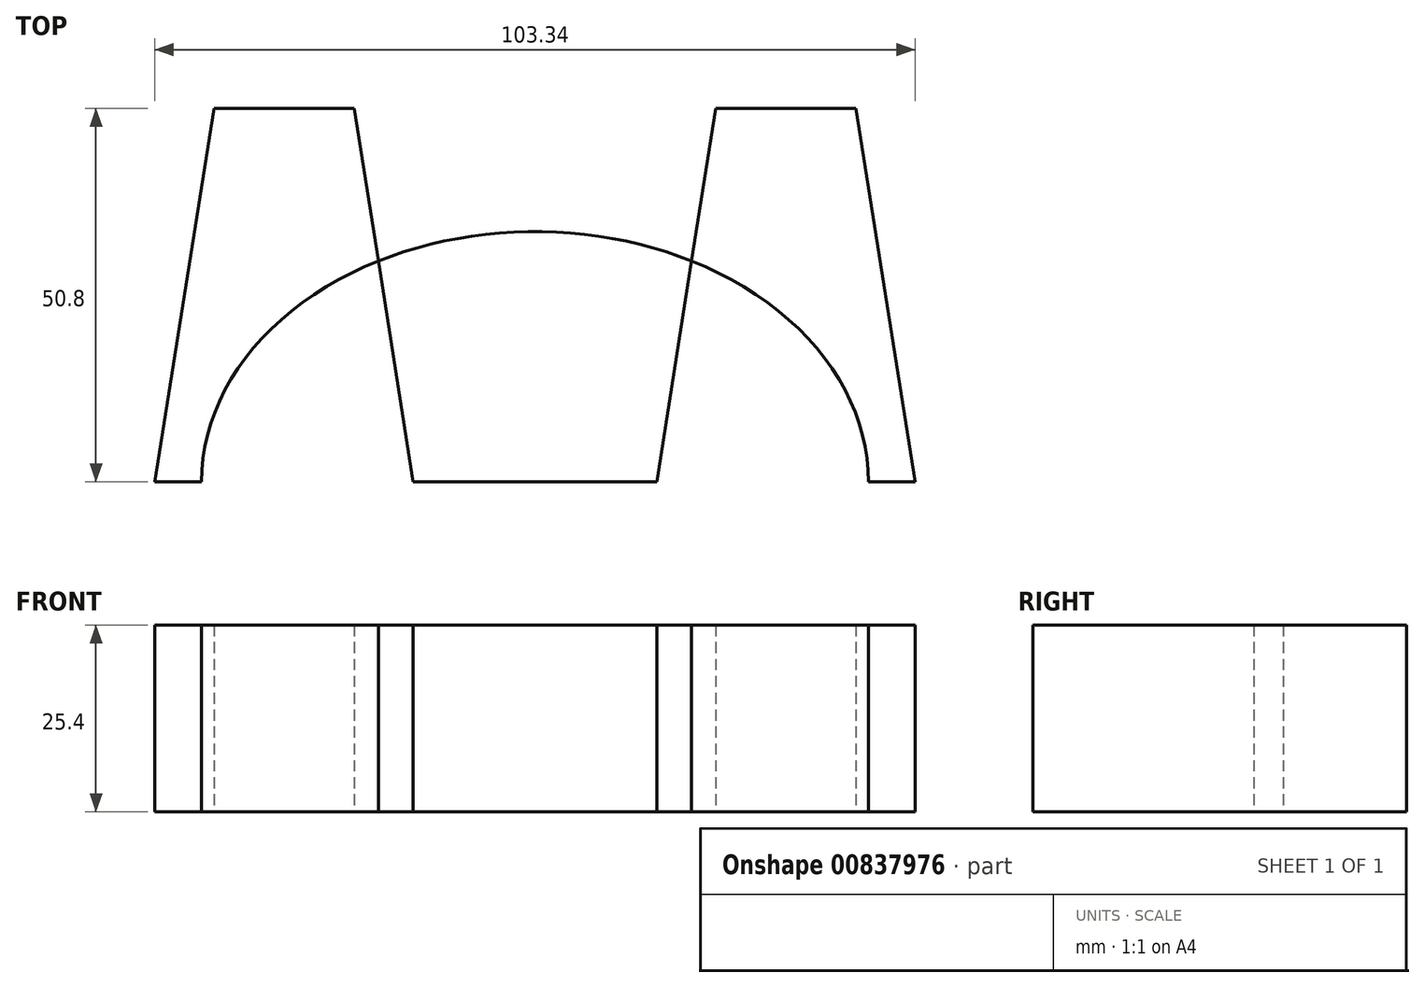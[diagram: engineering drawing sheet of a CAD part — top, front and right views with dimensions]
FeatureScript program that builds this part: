
annotation { "Feature Type Name" : "Feature", "Feature Type Description" : "" }
export const myFeature = defineFeature(function(context is Context, id is Id, definition is map)
    precondition{}
    {
        {
            var Q0;
            Q0=qCreatedBy(makeId("Top.planeOp"),FACE);
            var sketch = newSketch(context, id + "F0", { "sketchPlane" : qUnion([Q0])});
            skLineSegment(sketch, "E0", {"start": v(-51.67, 0) * mm, "end": v(-43.63, 50.8) * mm});
            skLineSegment(sketch, "E1", {"start": v(-43.63, 50.8) * mm, "end": v(-24.58, 50.8) * mm});
            skLineSegment(sketch, "E2", {"start": v(-24.58, 50.8) * mm, "end": v(-16.55, 0) * mm});
            skLineSegment(sketch, "E3", {"start": v(-16.55, 0) * mm, "end": v(-51.67, 0) * mm});
            skLineSegment(sketch, "E4.MirrorCS", {"start": v(43.63, 50.8) * mm, "end": v(24.58, 50.8) * mm});
            skLineSegment(sketch, "E5.MirrorCS", {"start": v(24.58, 50.8) * mm, "end": v(16.55, 0) * mm});
            skLineSegment(sketch, "E6.MirrorCS", {"start": v(16.55, 0) * mm, "end": v(51.67, 0) * mm});
            skLineSegment(sketch, "E7.MirrorCS", {"start": v(51.67, 0) * mm, "end": v(43.63, 50.8) * mm});
            skLineSegment(sketch, "E8", {"start": v(-16.55, 0) * mm, "end": v(16.55, 0) * mm});
            skEllipse(sketch, "E9", {"center": v(0, 0) * mm, "majorRadius": 45.32 * mm, "minorRadius": 34.03 * mm, "majorAxis": v(1, 0)});
            skPoint(sketch, "E10", {"position": v(-45.32, 0) * mm});
            skLineSegment(sketch, "E11", {"start": v(-43.63, 50.8) * mm, "end": v(-43.63, 0) * mm, "construction": true});
            skLineSegment(sketch, "E12", {"start": v(-24.58, 50.8) * mm, "end": v(-24.58, 0) * mm, "construction": true});
            skLineSegment(sketch, "E13", {"start": v(-51.67, 0) * mm, "end": v(-43.63, 0) * mm, "construction": true});
            skLineSegment(sketch, "E14", {"start": v(-24.58, 0) * mm, "end": v(-16.55, 0) * mm, "construction": true});
            skSolve(sketch);
        }
        {
            var Q0;
            {var subQ0=sQuery(id+"F0.wireOp",EDGE,"E0");Q0=makeQuery(id+"F0.imprint","IMPRINT",FACE,{"disambiguationData":[TD([[makeQuery(id+"F0.imprint","IMPRINT",EDGE,{"derivedFrom":subQ0}),-1.0]])]});}
            var Q1;
            {var subQ1=sQuery(id+"F0.wireOp",EDGE,"E2");Q1=makeQuery(id+"F0.imprint","IMPRINT",FACE,{"disambiguationData":[TD([[makeQuery(id+"F0.imprint","IMPRINT",EDGE,{"derivedFrom":subQ1}),1.0]])]});}
            var Q2;
            {var subQ0=sQuery(id+"F0.wireOp",EDGE,"E7.MirrorCS");Q2=makeQuery(id+"F0.imprint","IMPRINT",FACE,{"disambiguationData":[TD([[makeQuery(id+"F0.imprint","IMPRINT",EDGE,{"derivedFrom":subQ0}),1.0]])]});}
            extrude(context, id + "F1", {"entities" : qUnion([Q0, Q1, Q2]), "depth" : 25.4 * mm, "offsetDistance" : 25.4 * mm});
        }
    });
